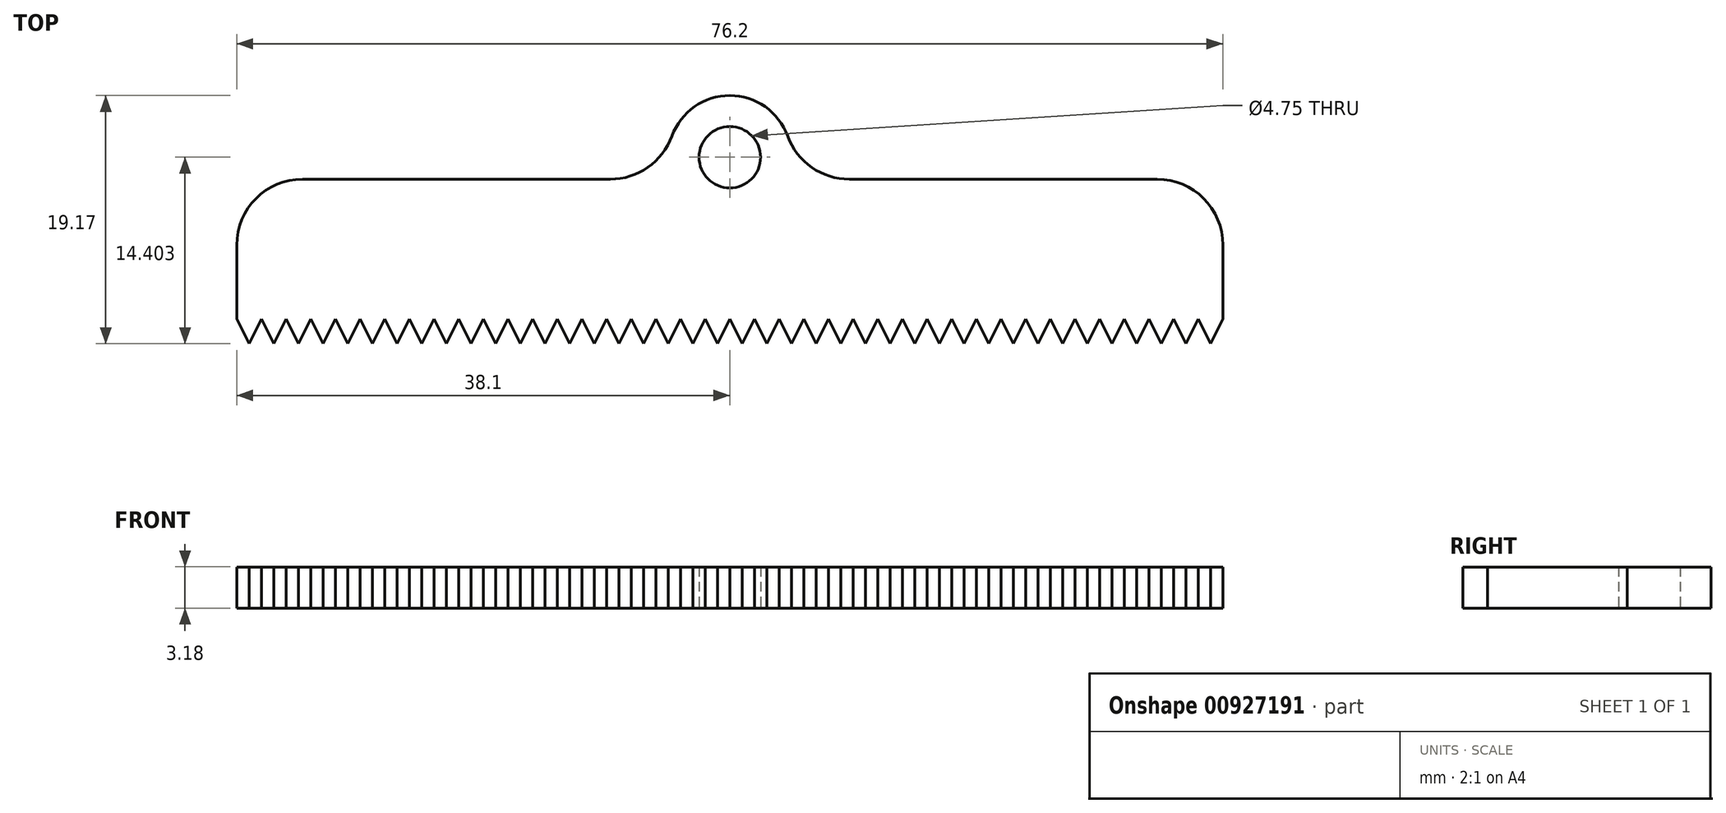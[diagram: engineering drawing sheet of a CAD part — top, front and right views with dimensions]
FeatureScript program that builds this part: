
annotation { "Feature Type Name" : "Feature", "Feature Type Description" : "" }
export const myFeature = defineFeature(function(context is Context, id is Id, definition is map)
    precondition{}
    {
        {
            var Q0;
            Q0=qCreatedBy(makeId("Top.planeOp"),FACE);
            var sketch = newSketch(context, id + "F0", { "sketchPlane" : qUnion([Q0])});
            skLineSegment(sketch, "E0.bottom", {"start": v(38.1, -9.52) * mm, "end": v(-38.1, -9.53) * mm});
            skLineSegment(sketch, "E0.left", {"start": v(38.1, -9.52) * mm, "end": v(38.1, -1.9) * mm});
            skLineSegment(sketch, "E0.right", {"start": v(-38.1, -9.53) * mm, "end": v(-38.1, -1.9) * mm});
            skPoint(sketch, "E0.middle", {"position": v(0, 0) * mm});
            skLineSegment(sketch, "E1", {"start": v(-33.02, 3.17) * mm, "end": v(-9.24, 3.17) * mm});
            skPoint(sketch, "E2.orphan", {"position": v(-38.1, 9.52) * mm});
            skPoint(sketch, "E3.orphan", {"position": v(38.1, 9.53) * mm});
            skLineSegment(sketch, "E4.trimOffspring", {"start": v(9.24, 3.17) * mm, "end": v(33.02, 3.17) * mm});
            skPoint(sketch, "E5.visualSharp", {"position": v(-38.1, 3.17) * mm});
            skArc(sketch, "E5.filletArc", {"start": v(-33.02, 3.18) * mm, "mid": v(-36.61, 1.69) * mm, "end": v(-38.1, -1.9) * mm});
            skPoint(sketch, "E6.visualSharp", {"position": v(38.1, 3.17) * mm});
            skArc(sketch, "E6.filletArc", {"start": v(38.1, -1.9) * mm, "mid": v(36.61, 1.69) * mm, "end": v(33.02, 3.18) * mm});
            skCircle(sketch, "E7", {"center": v(0, 4.87) * mm, "radius": 2.37 * mm});
            skArc(sketch, "E8", {"start": v(4.47, 6.5) * mm, "mid": v(0, 9.64) * mm, "end": v(-4.47, 6.5) * mm});
            skPoint(sketch, "E9.visualSharp", {"position": v(-4.45, 3.18) * mm});
            skArc(sketch, "E9.filletArc", {"start": v(-9.24, 3.18) * mm, "mid": v(-6.33, 4.1) * mm, "end": v(-4.47, 6.5) * mm});
            skPoint(sketch, "E10.visualSharp", {"position": v(4.45, 3.18) * mm});
            skArc(sketch, "E10.filletArc", {"start": v(4.47, 6.5) * mm, "mid": v(6.33, 4.1) * mm, "end": v(9.24, 3.17) * mm});
            skSolve(sketch);
        }
        {
            var Q0;
            Q0=makeQuery(id+"F0.imprint","IMPRINT",FACE,{"disambiguationData":[TD([[makeQuery(id+"F0.imprint","IMPRINT",EDGE,{"derivedFrom":sQuery(id+"F0.wireOp",EDGE,"E0.bottom")}),-1.0]])]});
            extrude(context, id + "F1", {"entities" : qUnion([Q0]), "depth" : 3.17 * mm, "offsetDistance" : 25.4 * mm});
        }
        {
            var Q0;
            Q0=makeQuery(id+"F1.opExtrude","CAP_FACE",FACE,{"disambiguationData":[OSD([sQuery(id+"F0.wireOp",EDGE,"E0.bottom"),sQuery(id+"F0.wireOp",EDGE,"E0.left"),sQuery(id+"F0.wireOp",EDGE,"E0.right"),sQuery(id+"F0.wireOp",EDGE,"E1"),sQuery(id+"F0.wireOp",EDGE,"E4.trimOffspring"),sQuery(id+"F0.wireOp",EDGE,"E5.filletArc"),sQuery(id+"F0.wireOp",EDGE,"E6.filletArc"),sQuery(id+"F0.wireOp",EDGE,"E7"),sQuery(id+"F0.wireOp",EDGE,"E8"),sQuery(id+"F0.wireOp",EDGE,"E9.filletArc"),sQuery(id+"F0.wireOp",EDGE,"E10.filletArc")])],"isStart":false});
            var sketch = newSketch(context, id + "F2", { "sketchPlane" : qUnion([Q0])});
            skLineSegment(sketch, "E11.top", {"start": v(-38.1, -14.15) * mm, "end": v(38.1, -14.15) * mm});
            skLineSegment(sketch, "E11.left", {"start": v(-38.1, -7.62) * mm, "end": v(-38.1, -14.15) * mm});
            skLineSegment(sketch, "E11.right", {"start": v(38.1, -7.62) * mm, "end": v(38.1, -14.15) * mm});
            skLineSegment(sketch, "E12", {"start": v(-38.1, -7.62) * mm, "end": v(-37.15, -9.52) * mm});
            skLineSegment(sketch, "E13", {"start": v(-38.1, -7.62) * mm, "end": v(-39.05, -9.53) * mm});
            skLineSegment(sketch, "E14.1.0.0", {"start": v(-36.2, -7.62) * mm, "end": v(-35.24, -9.52) * mm});
            skLineSegment(sketch, "E14.1.0.1", {"start": v(-36.2, -7.62) * mm, "end": v(-37.15, -9.53) * mm});
            skLineSegment(sketch, "E14.2.0.0", {"start": v(-34.29, -7.62) * mm, "end": v(-33.34, -9.52) * mm});
            skLineSegment(sketch, "E14.2.0.1", {"start": v(-34.29, -7.62) * mm, "end": v(-35.24, -9.53) * mm});
            skLineSegment(sketch, "E14.3.0.0", {"start": v(-32.38, -7.62) * mm, "end": v(-31.43, -9.52) * mm});
            skLineSegment(sketch, "E14.3.0.1", {"start": v(-32.38, -7.62) * mm, "end": v(-33.34, -9.53) * mm});
            skLineSegment(sketch, "E14.4.0.0", {"start": v(-30.48, -7.62) * mm, "end": v(-29.53, -9.53) * mm});
            skLineSegment(sketch, "E14.4.0.1", {"start": v(-30.48, -7.62) * mm, "end": v(-31.43, -9.53) * mm});
            skLineSegment(sketch, "E14.5.0.0", {"start": v(-28.57, -7.62) * mm, "end": v(-27.62, -9.53) * mm});
            skLineSegment(sketch, "E14.5.0.1", {"start": v(-28.57, -7.62) * mm, "end": v(-29.53, -9.53) * mm});
            skLineSegment(sketch, "E14.6.0.0", {"start": v(-26.67, -7.62) * mm, "end": v(-25.72, -9.53) * mm});
            skLineSegment(sketch, "E14.6.0.1", {"start": v(-26.67, -7.62) * mm, "end": v(-27.62, -9.53) * mm});
            skLineSegment(sketch, "E14.7.0.0", {"start": v(-24.76, -7.62) * mm, "end": v(-23.81, -9.53) * mm});
            skLineSegment(sketch, "E14.7.0.1", {"start": v(-24.76, -7.62) * mm, "end": v(-25.72, -9.53) * mm});
            skLineSegment(sketch, "E14.8.0.0", {"start": v(-22.86, -7.62) * mm, "end": v(-21.9, -9.53) * mm});
            skLineSegment(sketch, "E14.8.0.1", {"start": v(-22.86, -7.62) * mm, "end": v(-23.81, -9.53) * mm});
            skLineSegment(sketch, "E14.9.0.0", {"start": v(-20.95, -7.62) * mm, "end": v(-20, -9.53) * mm});
            skLineSegment(sketch, "E14.9.0.1", {"start": v(-20.95, -7.62) * mm, "end": v(-21.9, -9.53) * mm});
            skLineSegment(sketch, "E14.10.0.0", {"start": v(-19.05, -7.62) * mm, "end": v(-18.1, -9.53) * mm});
            skLineSegment(sketch, "E14.10.0.1", {"start": v(-19.05, -7.62) * mm, "end": v(-20, -9.53) * mm});
            skLineSegment(sketch, "E14.11.0.0", {"start": v(-17.14, -7.62) * mm, "end": v(-16.2, -9.53) * mm});
            skLineSegment(sketch, "E14.11.0.1", {"start": v(-17.14, -7.62) * mm, "end": v(-18.1, -9.53) * mm});
            skLineSegment(sketch, "E14.12.0.0", {"start": v(-15.24, -7.62) * mm, "end": v(-14.29, -9.53) * mm});
            skLineSegment(sketch, "E14.12.0.1", {"start": v(-15.24, -7.62) * mm, "end": v(-16.2, -9.53) * mm});
            skLineSegment(sketch, "E14.13.0.0", {"start": v(-13.33, -7.62) * mm, "end": v(-12.38, -9.53) * mm});
            skLineSegment(sketch, "E14.13.0.1", {"start": v(-13.33, -7.62) * mm, "end": v(-14.29, -9.53) * mm});
            skLineSegment(sketch, "E14.14.0.0", {"start": v(-11.43, -7.62) * mm, "end": v(-10.48, -9.53) * mm});
            skLineSegment(sketch, "E14.14.0.1", {"start": v(-11.43, -7.62) * mm, "end": v(-12.38, -9.53) * mm});
            skLineSegment(sketch, "E14.15.0.0", {"start": v(-9.52, -7.62) * mm, "end": v(-8.57, -9.53) * mm});
            skLineSegment(sketch, "E14.15.0.1", {"start": v(-9.52, -7.62) * mm, "end": v(-10.48, -9.53) * mm});
            skLineSegment(sketch, "E14.16.0.0", {"start": v(-7.62, -7.62) * mm, "end": v(-6.67, -9.53) * mm});
            skLineSegment(sketch, "E14.16.0.1", {"start": v(-7.62, -7.62) * mm, "end": v(-8.57, -9.53) * mm});
            skLineSegment(sketch, "E14.17.0.0", {"start": v(-5.71, -7.62) * mm, "end": v(-4.76, -9.53) * mm});
            skLineSegment(sketch, "E14.17.0.1", {"start": v(-5.71, -7.62) * mm, "end": v(-6.67, -9.53) * mm});
            skLineSegment(sketch, "E14.18.0.0", {"start": v(-3.8, -7.62) * mm, "end": v(-2.86, -9.53) * mm});
            skLineSegment(sketch, "E14.18.0.1", {"start": v(-3.8, -7.62) * mm, "end": v(-4.76, -9.53) * mm});
            skLineSegment(sketch, "E14.19.0.0", {"start": v(-1.9, -7.62) * mm, "end": v(-0.95, -9.53) * mm});
            skLineSegment(sketch, "E14.19.0.1", {"start": v(-1.9, -7.62) * mm, "end": v(-2.86, -9.53) * mm});
            skLineSegment(sketch, "E14.20.0.0", {"start": v(0, -7.62) * mm, "end": v(0.95, -9.53) * mm});
            skLineSegment(sketch, "E14.20.0.1", {"start": v(0, -7.62) * mm, "end": v(-0.95, -9.53) * mm});
            skLineSegment(sketch, "E14.21.0.0", {"start": v(1.9, -7.62) * mm, "end": v(2.86, -9.53) * mm});
            skLineSegment(sketch, "E14.21.0.1", {"start": v(1.9, -7.62) * mm, "end": v(0.95, -9.53) * mm});
            skLineSegment(sketch, "E14.22.0.0", {"start": v(3.81, -7.62) * mm, "end": v(4.76, -9.53) * mm});
            skLineSegment(sketch, "E14.22.0.1", {"start": v(3.81, -7.62) * mm, "end": v(2.86, -9.53) * mm});
            skLineSegment(sketch, "E14.23.0.0", {"start": v(5.72, -7.62) * mm, "end": v(6.67, -9.53) * mm});
            skLineSegment(sketch, "E14.23.0.1", {"start": v(5.72, -7.62) * mm, "end": v(4.76, -9.53) * mm});
            skLineSegment(sketch, "E14.24.0.0", {"start": v(7.62, -7.62) * mm, "end": v(8.57, -9.52) * mm});
            skLineSegment(sketch, "E14.24.0.1", {"start": v(7.62, -7.62) * mm, "end": v(6.67, -9.53) * mm});
            skLineSegment(sketch, "E14.25.0.0", {"start": v(9.53, -7.62) * mm, "end": v(10.48, -9.53) * mm});
            skLineSegment(sketch, "E14.25.0.1", {"start": v(9.53, -7.62) * mm, "end": v(8.57, -9.53) * mm});
            skLineSegment(sketch, "E14.26.0.0", {"start": v(11.43, -7.62) * mm, "end": v(12.38, -9.52) * mm});
            skLineSegment(sketch, "E14.26.0.1", {"start": v(11.43, -7.62) * mm, "end": v(10.48, -9.53) * mm});
            skLineSegment(sketch, "E14.27.0.0", {"start": v(13.34, -7.62) * mm, "end": v(14.29, -9.53) * mm});
            skLineSegment(sketch, "E14.27.0.1", {"start": v(13.33, -7.62) * mm, "end": v(12.38, -9.53) * mm});
            skLineSegment(sketch, "E14.28.0.0", {"start": v(15.24, -7.62) * mm, "end": v(16.2, -9.52) * mm});
            skLineSegment(sketch, "E14.28.0.1", {"start": v(15.24, -7.62) * mm, "end": v(14.29, -9.53) * mm});
            skLineSegment(sketch, "E14.29.0.0", {"start": v(17.15, -7.62) * mm, "end": v(18.1, -9.53) * mm});
            skLineSegment(sketch, "E14.29.0.1", {"start": v(17.14, -7.62) * mm, "end": v(16.2, -9.53) * mm});
            skLineSegment(sketch, "E14.30.0.0", {"start": v(19.05, -7.62) * mm, "end": v(20, -9.52) * mm});
            skLineSegment(sketch, "E14.30.0.1", {"start": v(19.05, -7.62) * mm, "end": v(18.1, -9.53) * mm});
            skLineSegment(sketch, "E14.31.0.0", {"start": v(20.96, -7.62) * mm, "end": v(21.9, -9.53) * mm});
            skLineSegment(sketch, "E14.31.0.1", {"start": v(20.95, -7.62) * mm, "end": v(20, -9.53) * mm});
            skLineSegment(sketch, "E14.32.0.0", {"start": v(22.86, -7.62) * mm, "end": v(23.81, -9.52) * mm});
            skLineSegment(sketch, "E14.32.0.1", {"start": v(22.86, -7.62) * mm, "end": v(21.9, -9.53) * mm});
            skLineSegment(sketch, "E14.33.0.0", {"start": v(24.77, -7.62) * mm, "end": v(25.72, -9.53) * mm});
            skLineSegment(sketch, "E14.33.0.1", {"start": v(24.76, -7.62) * mm, "end": v(23.81, -9.53) * mm});
            skLineSegment(sketch, "E14.34.0.0", {"start": v(26.67, -7.62) * mm, "end": v(27.62, -9.53) * mm});
            skLineSegment(sketch, "E14.34.0.1", {"start": v(26.67, -7.62) * mm, "end": v(25.72, -9.53) * mm});
            skLineSegment(sketch, "E14.35.0.0", {"start": v(28.58, -7.62) * mm, "end": v(29.53, -9.53) * mm});
            skLineSegment(sketch, "E14.35.0.1", {"start": v(28.57, -7.62) * mm, "end": v(27.62, -9.53) * mm});
            skLineSegment(sketch, "E14.36.0.0", {"start": v(30.48, -7.62) * mm, "end": v(31.43, -9.53) * mm});
            skLineSegment(sketch, "E14.36.0.1", {"start": v(30.48, -7.62) * mm, "end": v(29.53, -9.53) * mm});
            skLineSegment(sketch, "E14.37.0.0", {"start": v(32.38, -7.62) * mm, "end": v(33.34, -9.53) * mm});
            skLineSegment(sketch, "E14.37.0.1", {"start": v(32.38, -7.62) * mm, "end": v(31.43, -9.53) * mm});
            skLineSegment(sketch, "E14.38.0.0", {"start": v(34.3, -7.62) * mm, "end": v(35.24, -9.52) * mm});
            skLineSegment(sketch, "E14.38.0.1", {"start": v(34.29, -7.62) * mm, "end": v(33.34, -9.53) * mm});
            skLineSegment(sketch, "E14.39.0.0", {"start": v(36.2, -7.62) * mm, "end": v(37.15, -9.53) * mm});
            skLineSegment(sketch, "E14.39.0.1", {"start": v(36.2, -7.62) * mm, "end": v(35.24, -9.53) * mm});
            skLineSegment(sketch, "E14.40.0.1", {"start": v(38.1, -7.62) * mm, "end": v(37.15, -9.53) * mm});
            skLineSegment(sketch, "E14.direction1", {"start": v(-39.05, -9.53) * mm, "end": v(-37.15, -9.53) * mm, "construction": true});
            skSolve(sketch);
        }
        {
            var Q0;
            Q0=qSketchRegion(id+"F2",true);
            extrude(context, id + "F3", {"entities" : qUnion([Q0]), "operationType" : NewBodyOperationType.REMOVE, "oppositeDirection" : true, "depth" : 25.4 * mm, "offsetDistance" : 25.4 * mm});
        }
    });
